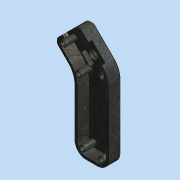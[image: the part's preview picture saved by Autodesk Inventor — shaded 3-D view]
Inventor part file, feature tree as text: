
AUTODESK INVENTOR PART (.ipt)
format: ipt  version: 2015 (Build 190159000, 159)  size: 302,080 bytes
history: native  units: in
note: dims shown in document units (in); Inventor stores cm internally (conversion verified against a paired STEP export)
features: extrude x9, sketch x7, projected_geometry x4, plane x2, shell x1, chamfer x1, fillet x1
ambient origin geometry x8: Origin, YZ Plane, XZ Plane, XY Plane, X Axis, Y Axis, Z Axis, Center Point
bodies: Solid1 (feature_tree), Solid2 (feature_tree)
feature tree (25):
  extrude  "Extrusion1"  Depth=1.5in
  shell  "Shell1"  Thickness=1.5in
  extrude  "Extrusion2"  Depth=1.25in
  sketch  "Sketch3"  dims[d5=1.0in d6=0.25in]
  extrude  "Extrusion3"  Depth=0.25in
  extrude  "Extrusion4"  Depth=0.625in TaperAngle=0.0deg
  sketch  "Sketch4"  dims[d7=0.5in d8=0.625in d9=0.0in]
  plane  "Work Plane1"
  extrude  "Extrusion5"  Depth=0.125in
  sketch  "Sketch5"  dims[d10=0.125in d11=0.75in]
  extrude  "Extrusion6"  Depth=0.5in TaperAngle=0.0deg
  extrude  "Extrusion7"  Depth=1.0625in
  chamfer  "Chamfer1"  Distance=0.5in
  sketch  "Sketch6"  dims[d12=0.1562in d13=0.5in d14=0.0in]
  plane  "Work Plane2"
  extrude  "Extrusion8"  Depth=0.125in TaperAngle=0.0deg
  extrude  "Extrusion9"  Depth=0.375in
  fillet  "Fillet1"  Radius=0.0312in
  sketch  "Sketch1"  dims[d0=45.0deg d1=1.5in d2=1.5in]
  sketch  "Sketch2"  dims[d3=3.0in d4=1.25in]
  projected_geometry  "Projected Loop1"
  projected_geometry  "Projected Loop2"
  projected_geometry  "Projected Loop3"
  sketch  "Sketch7"  dims[d15=1.0in d16=1.0625in d17=0.5in d18=0.0in d19=0.125in d20=0.0in d21=0.375in d23=0.0312in d24=0.0312in d25=0.0312in d26=0.0312in d27=-0.125in d28=0.125in d29=0.0in d30=0.2635in d31=0.201in d32=45.0deg d33=0.2635in d34=0.201in d35=0.2635in d36=0.201in d37=0.125in d38=0.0in d39=0.0in d40=0.0in d41=0.2635in d42=0.201in d45=0.125in d46=0.125in d47=45.0deg d48=0.25in d49=0.5in d50=-0.25in d51=0.125in d52=0.0in d53=0.0625in d54=0.5in d55=0.1875in d56=0.125in d57=0.0in d58=0.0625in]
  projected_geometry  "Projected Loop4"
